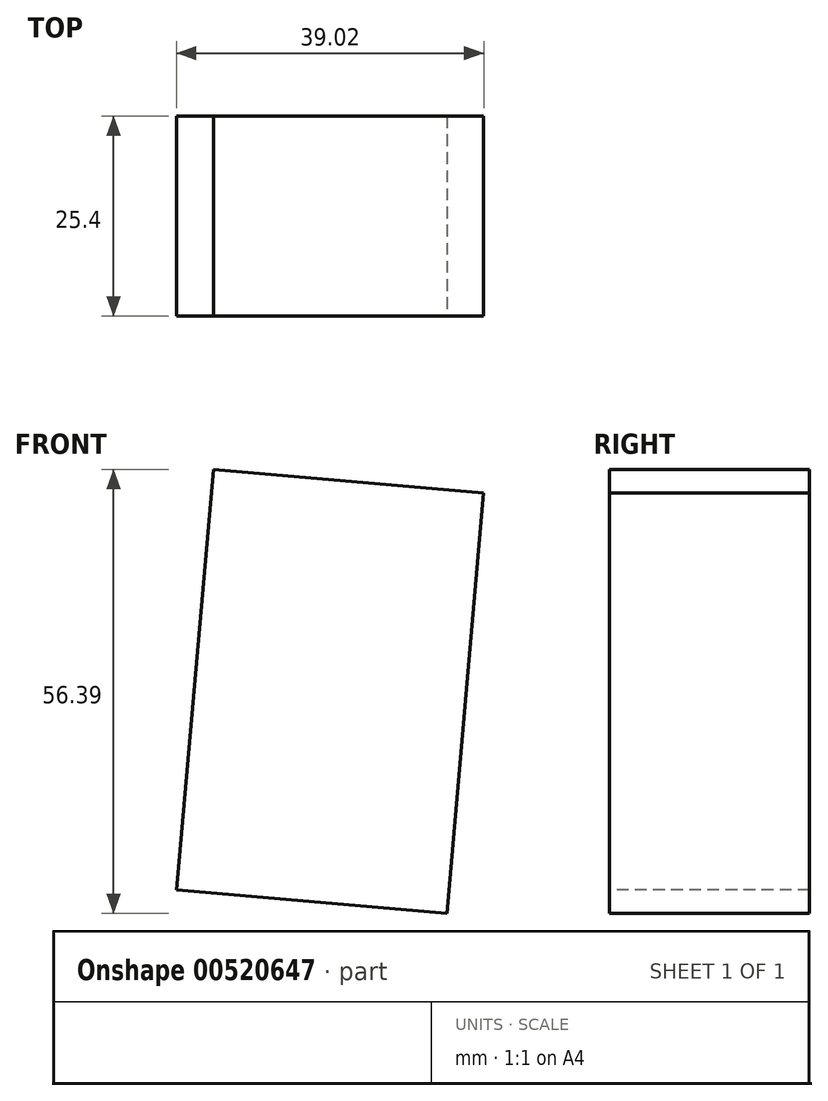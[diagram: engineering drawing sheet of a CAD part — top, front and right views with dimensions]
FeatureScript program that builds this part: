
annotation { "Feature Type Name" : "Feature", "Feature Type Description" : "" }
export const myFeature = defineFeature(function(context is Context, id is Id, definition is map)
    precondition{}
    {
        {
            var Q0;
            Q0=qCreatedBy(makeId("Front.planeOp"),FACE);
            var sketch = newSketch(context, id + "F0", { "sketchPlane" : qUnion([Q0])});
            skLineSegment(sketch, "E0.bottom", {"start": v(-0.13, -3) * mm, "end": v(-34.48, 0) * mm});
            skLineSegment(sketch, "E0.top", {"start": v(4.54, 50.37) * mm, "end": v(-29.8, 53.38) * mm});
            skLineSegment(sketch, "E0.left", {"start": v(-0.13, -3) * mm, "end": v(4.54, 50.37) * mm});
            skLineSegment(sketch, "E0.right", {"start": v(-34.48, 0) * mm, "end": v(-29.8, 53.38) * mm});
            skSolve(sketch);
        }
        {
            var Q0;
            Q0=makeQuery(id+"F0.imprint","IMPRINT",FACE,{"disambiguationData":[TD([[makeQuery(id+"F0.imprint","IMPRINT",EDGE,{"derivedFrom":sQuery(id+"F0.wireOp",EDGE,"E0.bottom")}),-1.0]])]});
            extrude(context, id + "F1", {"entities" : qUnion([Q0]), "oppositeDirection" : true, "depth" : 25.4 * mm, "offsetDistance" : 25.4 * mm});
        }
    });
